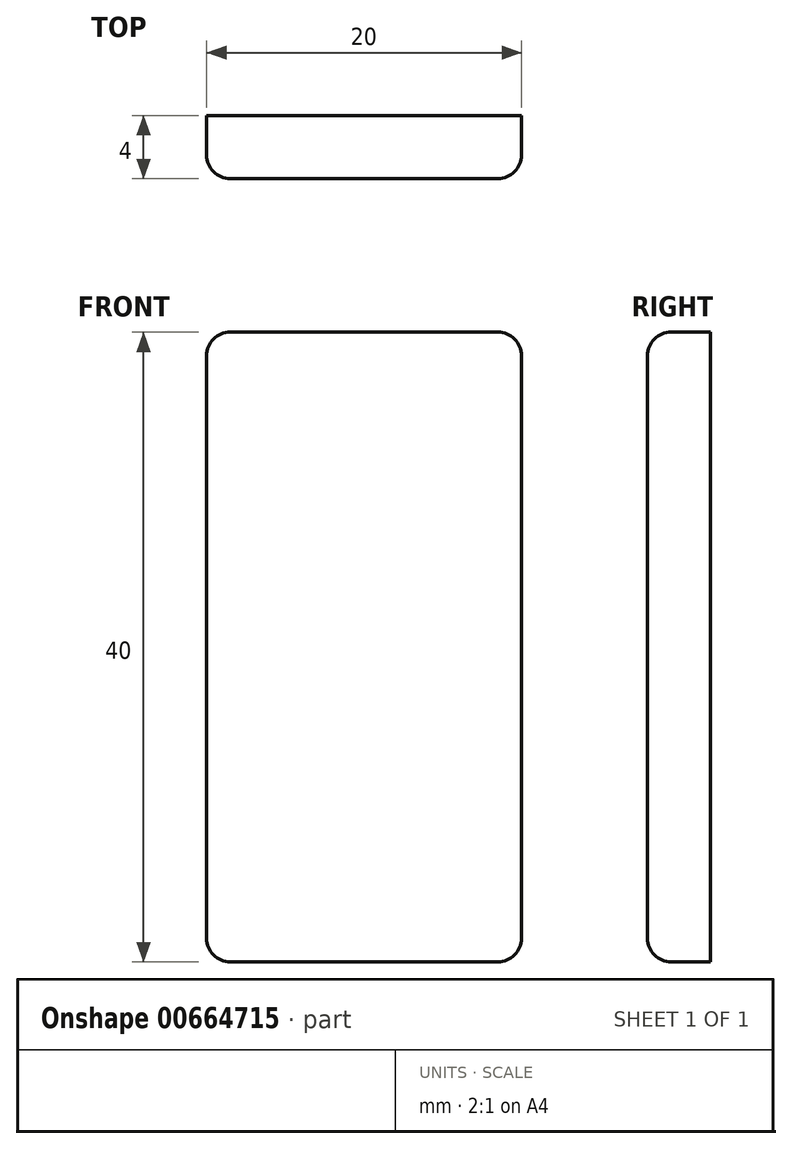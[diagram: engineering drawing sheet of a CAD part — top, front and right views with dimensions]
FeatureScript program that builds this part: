
annotation { "Feature Type Name" : "Feature", "Feature Type Description" : "" }
export const myFeature = defineFeature(function(context is Context, id is Id, definition is map)
    precondition{}
    {
        {
            var Q0;
            Q0=qCreatedBy(makeId("Front.planeOp"),FACE);
            var sketch = newSketch(context, id + "F0", { "sketchPlane" : qUnion([Q0])});
            skLineSegment(sketch, "E0.bottom", {"start": v(0, 0) * mm, "end": v(20, 0) * mm});
            skLineSegment(sketch, "E0.top", {"start": v(0, -40) * mm, "end": v(20, -40) * mm});
            skLineSegment(sketch, "E0.left", {"start": v(0, 0) * mm, "end": v(0, -40) * mm});
            skLineSegment(sketch, "E0.right", {"start": v(20, 0) * mm, "end": v(20, -40) * mm});
            skLineSegment(sketch, "E1", {"start": v(10, 0) * mm, "end": v(10, -40) * mm, "construction": true});
            skLineSegment(sketch, "E2.0", {"start": v(0, -10) * mm, "end": v(20, -10) * mm, "construction": true});
            skLineSegment(sketch, "E3.0", {"start": v(0, -30) * mm, "end": v(20, -30) * mm, "construction": true});
            skCircle(sketch, "E4", {"center": v(10, -10) * mm, "radius": 2.5 * mm});
            skCircle(sketch, "E5", {"center": v(10, -30) * mm, "radius": 2.5 * mm});
            skSolve(sketch);
        }
        {
            var Q0;
            Q0=sQuery(id+"F0.wireOp",EDGE,"E4");
            var Q1;
            Q1=sQuery(id+"F0.wireOp",EDGE,"E5");
            extrude(context, id + "F1", {"bodyType" : ToolBodyType.SURFACE, "surfaceEntities" : qUnion([Q0, Q1]), "depth" : -6 * mm, "offsetDistance" : 25 * mm});
        }
        {
            var Q0;
            Q0=sQuery(id+"F0.wireOp",EDGE,"E4");
            var Q1;
            Q1=sQuery(id+"F0.wireOp",EDGE,"E5");
            extrude(context, id + "F2", {"bodyType" : ToolBodyType.SURFACE, "surfaceEntities" : qUnion([Q0, Q1]), "depth" : -6 * mm, "offsetDistance" : 25 * mm});
        }
        {
            var Q0;
            Q0=makeQuery(id+"F0.imprint","IMPRINT",FACE,{"disambiguationData":[TD([[makeQuery(id+"F0.imprint","IMPRINT",EDGE,{"derivedFrom":sQuery(id+"F0.wireOp",EDGE,"E0.bottom")}),-1.0]])]});
            var Q1;
            Q1=makeQuery(id+"F0.imprint","IMPRINT",FACE,{"disambiguationData":[TD([[makeQuery(id+"F0.imprint","IMPRINT",EDGE,{"derivedFrom":sQuery(id+"F0.wireOp",EDGE,"E4")}),1.0]])]});
            var Q2;
            Q2=makeQuery(id+"F0.imprint","IMPRINT",FACE,{"disambiguationData":[TD([[makeQuery(id+"F0.imprint","IMPRINT",EDGE,{"derivedFrom":sQuery(id+"F0.wireOp",EDGE,"E5")}),1.0]])]});
            extrude(context, id + "F3", {"entities" : qUnion([Q0, Q1, Q2]), "depth" : 4 * mm, "offsetDistance" : 25 * mm});
        }
        {
            var Q0;
            Q0=makeQuery(id+"F3.opExtrude","SWEPT_EDGE",EDGE,{"disambiguationData":[OSD([sQuery(id+"F0.wireOp",EDGE,"E0.bottom"),sQuery(id+"F0.wireOp",EDGE,"E0.left")])]});
            var Q1;
            Q1=makeQuery(id+"F3.opExtrude","CAP_EDGE",EDGE,{"disambiguationData":[OSD([sQuery(id+"F0.wireOp",EDGE,"E0.left")])],"isStart":false});
            var Q2;
            Q2=makeQuery(id+"F3.opExtrude","SWEPT_EDGE",EDGE,{"disambiguationData":[OSD([sQuery(id+"F0.wireOp",EDGE,"E0.top"),sQuery(id+"F0.wireOp",EDGE,"E0.left")])]});
            var Q3;
            Q3=makeQuery(id+"F3.opExtrude","CAP_EDGE",EDGE,{"disambiguationData":[OSD([sQuery(id+"F0.wireOp",EDGE,"E0.top")])],"isStart":false});
            var Q4;
            Q4=makeQuery(id+"F3.opExtrude","SWEPT_EDGE",EDGE,{"disambiguationData":[OSD([sQuery(id+"F0.wireOp",EDGE,"E0.top"),sQuery(id+"F0.wireOp",EDGE,"E0.right")])]});
            var Q5;
            Q5=makeQuery(id+"F3.opExtrude","CAP_EDGE",EDGE,{"disambiguationData":[OSD([sQuery(id+"F0.wireOp",EDGE,"E0.right")])],"isStart":false});
            var Q6;
            Q6=makeQuery(id+"F3.opExtrude","CAP_EDGE",EDGE,{"disambiguationData":[OSD([sQuery(id+"F0.wireOp",EDGE,"E0.bottom")])],"isStart":false});
            var Q7;
            Q7=makeQuery(id+"F3.opExtrude","SWEPT_EDGE",EDGE,{"disambiguationData":[OSD([sQuery(id+"F0.wireOp",EDGE,"E0.bottom"),sQuery(id+"F0.wireOp",EDGE,"E0.right")])]});
            fillet(context, id + "F4", {"entities" : qUnion([Q0, Q1, Q2, Q3, Q4, Q5, Q6, Q7]), "radius" : 1.5 * mm, "tangentPropagation" : true, "allowEdgeOverflow" : false});
        }
    });
